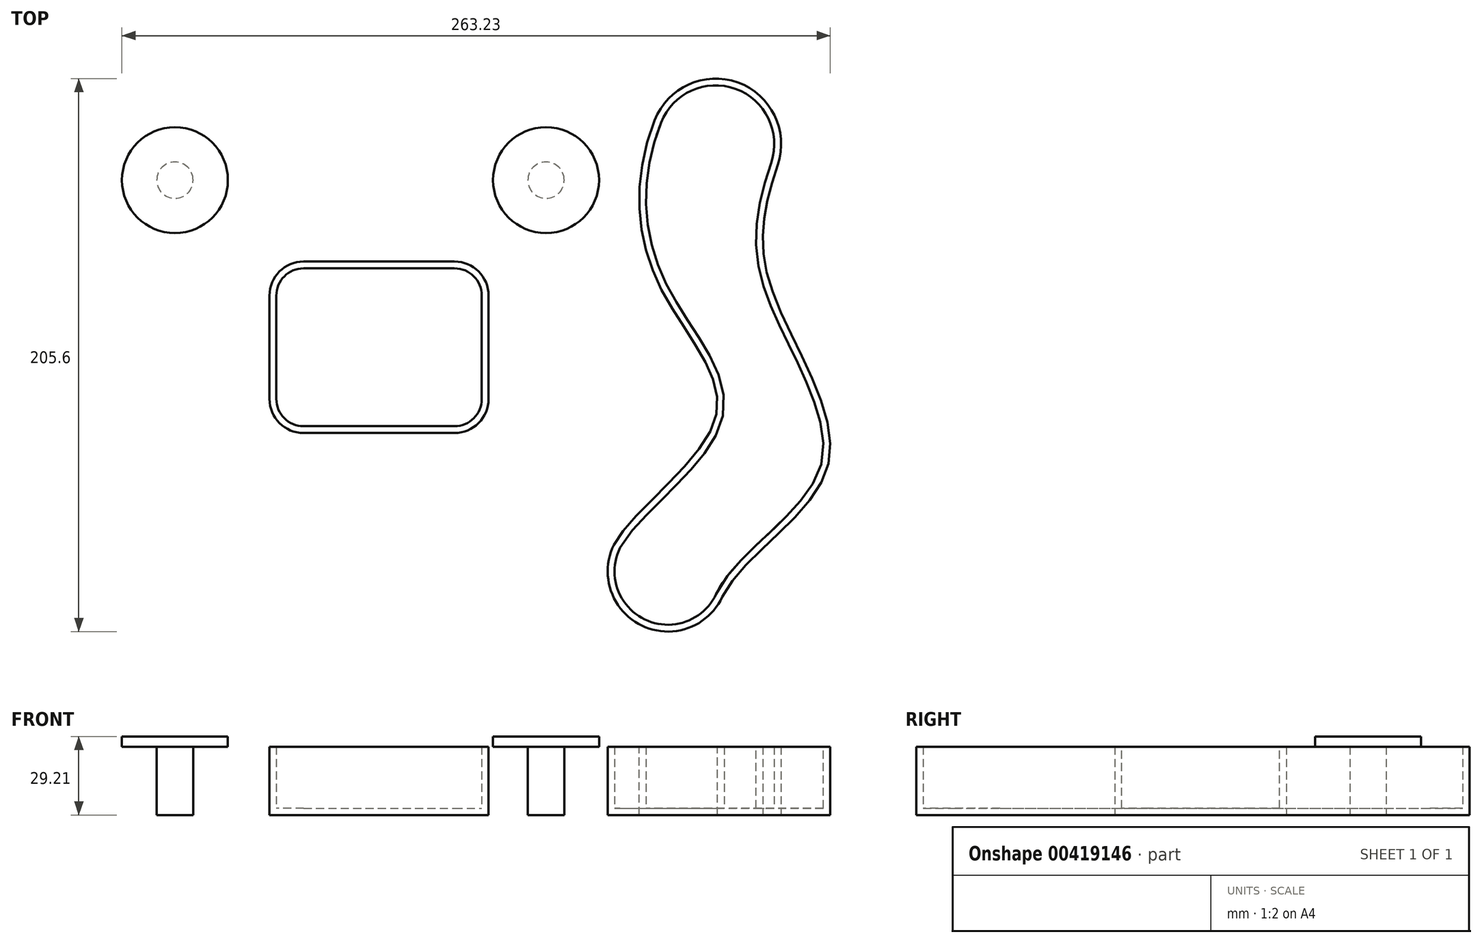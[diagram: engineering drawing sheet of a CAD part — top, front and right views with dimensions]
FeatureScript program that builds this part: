
annotation { "Feature Type Name" : "Feature", "Feature Type Description" : "" }
export const myFeature = defineFeature(function(context is Context, id is Id, definition is map)
    precondition{}
    {
        {
            var Q0;
            Q0=qCreatedBy(makeId("Top.planeOp"),FACE);
            var sketch = newSketch(context, id + "F0", { "sketchPlane" : qUnion([Q0])});
            skLineSegment(sketch, "E0.bottom", {"start": v(-107.67, 25.91) * mm, "end": v(-51.63, 25.91) * mm});
            skLineSegment(sketch, "E0.top", {"start": v(-107.67, -37.88) * mm, "end": v(-51.63, -37.88) * mm});
            skLineSegment(sketch, "E0.left", {"start": v(-120.37, 13.21) * mm, "end": v(-120.37, -25.18) * mm});
            skLineSegment(sketch, "E0.right", {"start": v(-38.93, 13.21) * mm, "end": v(-38.93, -25.18) * mm});
            skPoint(sketch, "E1.visualSharp", {"position": v(-120.37, -37.88) * mm});
            skArc(sketch, "E1.filletArc", {"start": v(-120.37, -25.18) * mm, "mid": v(-116.65, -34.16) * mm, "end": v(-107.67, -37.88) * mm});
            skPoint(sketch, "E2.visualSharp", {"position": v(-120.37, 25.91) * mm});
            skArc(sketch, "E2.filletArc", {"start": v(-107.67, 25.91) * mm, "mid": v(-116.65, 22.2) * mm, "end": v(-120.37, 13.21) * mm});
            skPoint(sketch, "E3.visualSharp", {"position": v(-38.93, 25.91) * mm});
            skArc(sketch, "E3.filletArc", {"start": v(-38.93, 13.21) * mm, "mid": v(-42.65, 22.2) * mm, "end": v(-51.63, 25.91) * mm});
            skPoint(sketch, "E4.visualSharp", {"position": v(-38.93, -37.88) * mm});
            skArc(sketch, "E4.filletArc", {"start": v(-51.63, -37.88) * mm, "mid": v(-42.65, -34.16) * mm, "end": v(-38.93, -25.18) * mm});
            skCircle(sketch, "E5", {"center": v(-17.59, 56.17) * mm, "radius": 6.76 * mm});
            skFitSpline(sketch, "E6", {"points": [v(47.94, -98.82) * mm, v(87.2, -49.77) * mm, v(65.96, 16.48) * mm, v(68.52, 61.96) * mm], "startDerivative": vector(65.4, 139.2) * mm, "endDerivative": vector(53.22, 160.46) * mm});
            skArc(sketch, "E7", {"start": v(7.64, -79.42) * mm, "mid": v(18, -109.46) * mm, "end": v(47.94, -98.82) * mm});
            skArc(sketch, "E8", {"start": v(22.8, 78.45) * mm, "mid": v(53.7, 92.48) * mm, "end": v(68.52, 61.96) * mm});
            skFitSpline(sketch, "E9", {"points": [v(7.64, -79.42) * mm, v(45.47, -31.95) * mm, v(25.15, 15.7) * mm, v(22.8, 78.45) * mm], "startDerivative": vector(55.82, 113.25) * mm, "endDerivative": vector(75.44, 193.28) * mm});
            skSolve(sketch);
        }
        {
            var Q0;
            Q0 = qSketchRegion(id + "F0", true);
            extrude(context, id + "F1", {"entities" : qUnion([Q0]), "depth" : 25.4 * mm});
        }
        {
            var Q0;
            Q0=makeQuery(id+"F1.opExtrude","CAP_FACE",FACE,{"disambiguationData":[OSD([sQuery(id+"F0.wireOp",EDGE,"E0.bottom"),sQuery(id+"F0.wireOp",EDGE,"E0.top"),sQuery(id+"F0.wireOp",EDGE,"E0.left"),sQuery(id+"F0.wireOp",EDGE,"E0.right"),sQuery(id+"F0.wireOp",EDGE,"E1.filletArc"),sQuery(id+"F0.wireOp",EDGE,"E2.filletArc"),sQuery(id+"F0.wireOp",EDGE,"E3.filletArc"),sQuery(id+"F0.wireOp",EDGE,"E4.filletArc")])],"isStart":false});
            var Q1;
            Q1=makeQuery(id+"F1.opExtrude","CAP_FACE",FACE,{"disambiguationData":[OSD([sQuery(id+"F0.wireOp",EDGE,"E6"),sQuery(id+"F0.wireOp",EDGE,"E7"),sQuery(id+"F0.wireOp",EDGE,"E8"),sQuery(id+"F0.wireOp",EDGE,"E9")])],"isStart":false});
            shell(context, id + "F2", {"entities" : qUnion([Q0, Q1]), "thickness" : 2.54 * mm});
        }
        {
            var Q0;
            Q0=makeQuery(id+"F1.opExtrude","CAP_FACE",FACE,{"disambiguationData":[OSD([sQuery(id+"F0.wireOp",EDGE,"E5")])],"isStart":false});
            var sketch = newSketch(context, id + "F3", { "sketchPlane" : qUnion([Q0])});
            skCircle(sketch, "E10", {"center": v(-17.59, 56.17) * mm, "radius": 19.69 * mm});
            skSolve(sketch);
        }
        {
            var Q0;
            Q0 = qSketchRegion(id + "F3", true);
            extrude(context, id + "F4", {"entities" : qUnion([Q0]), "operationType" : NewBodyOperationType.ADD, "depth" : 3.8 * mm});
        }
        {
            var Q0;
            Q0=makeQuery(id+"F1.opExtrude","SWEPT_BODY",BODY,{"disambiguationData":[OSD([sQuery(id+"F0.wireOp",EDGE,"E5")])]});
            transform(context, id + "F5", {"entities" : qUnion([Q0]), "transformType" : TransformType.TRANSLATION_3D, "dx" : -137.92 * mm, "dy" : 0 * mm, "dz" : 0 * mm, "makeCopy" : true});
        }
    });
